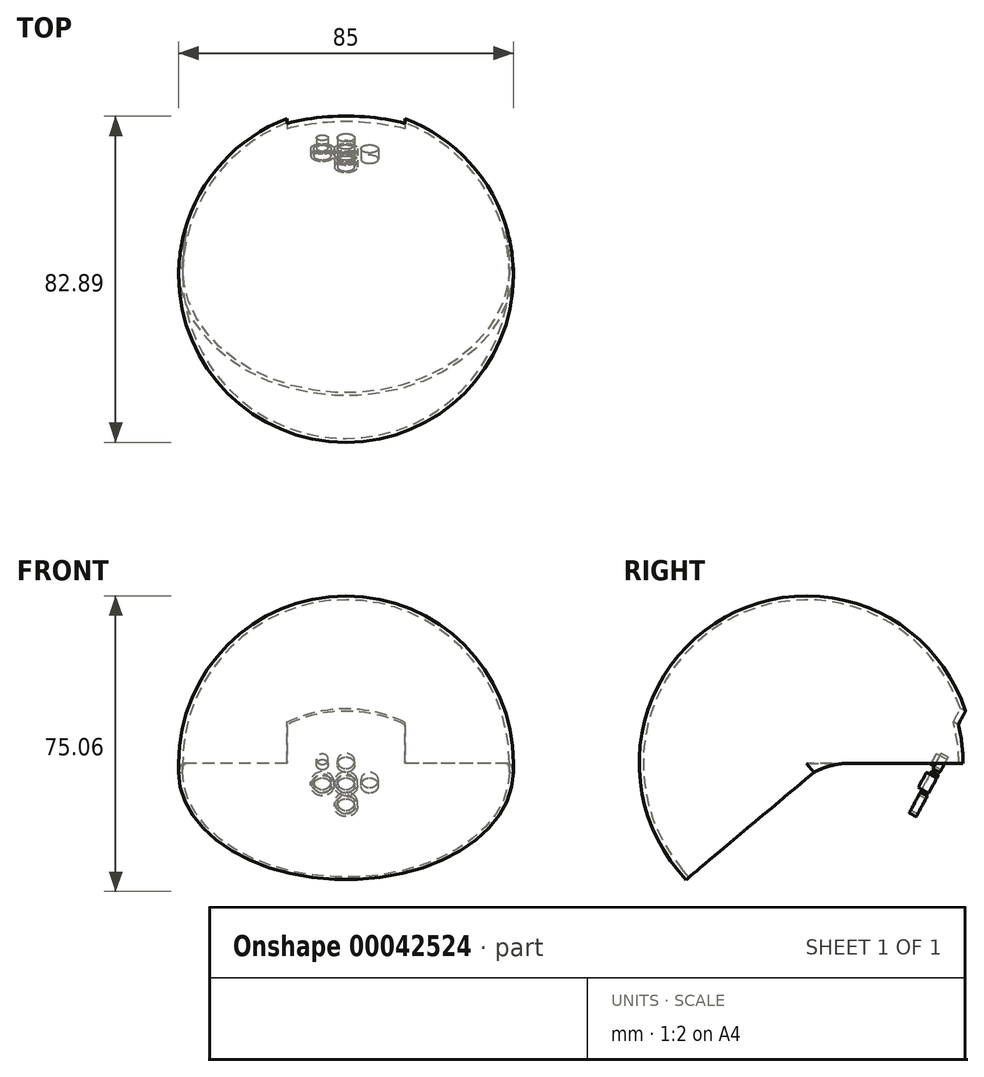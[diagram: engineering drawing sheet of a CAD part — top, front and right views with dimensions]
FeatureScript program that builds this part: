
annotation { "Feature Type Name" : "Feature", "Feature Type Description" : "" }
export const myFeature = defineFeature(function(context is Context, id is Id, definition is map)
    precondition{}
    {
        {
            var Q0;
            Q0=qCreatedBy(makeId("Top.planeOp"),FACE);
            var sketch = newSketch(context, id + "F0", { "sketchPlane" : qUnion([Q0])});
            skArc(sketch, "E0", {"start": v(42.5, 0) * mm, "mid": v(0, 42.5) * mm, "end": v(-42.5, 0) * mm});
            skLineSegment(sketch, "E1", {"start": v(-57, 0) * mm, "end": v(51.83, 0) * mm});
            skSolve(sketch);
        }
        {
            var Q0;
            {var subQ1=sQuery(id+"F0.wireOp",EDGE,"E0");Q0=makeQuery(id+"F0.imprint","IMPRINT",FACE,{"disambiguationData":[TD([[makeQuery(id+"F0.imprint","IMPRINT",EDGE,{"derivedFrom":subQ1}),1.0]])]});}
            var Q1;
            Q1=sQuery(id+"F0.wireOp",EDGE,"E1");
            revolve(context, id + "F1", {"entities" : qUnion([Q0]), "axis" : qUnion([Q1]), "revolveType" : RevolveType.ONE_DIRECTION, "angle" : 220 * degree});
        }
        {
            var Q0;
            Q0=makeQuery(id+"F1.opRevolve","CAP_FACE",FACE,{"disambiguationData":[OSD([sQuery(id+"F0.wireOp",EDGE,"E0"),sQuery(id+"F0.wireOp",EDGE,"E1")])],"isStart":true});
            var Q1;
            Q1=makeQuery(id+"F1.opRevolve","CAP_FACE",FACE,{"disambiguationData":[OSD([sQuery(id+"F0.wireOp",EDGE,"E0"),sQuery(id+"F0.wireOp",EDGE,"E1")])],"isStart":false});
            shell(context, id + "F2", {"entities" : qUnion([Q0, Q1]), "thickness" : 1 * mm});
        }
        {
            var Q0;
            Q0=makeQuery(id+"F1.opRevolve","CAP_FACE",FACE,{"disambiguationData":[OSD([sQuery(id+"F0.wireOp",EDGE,"E0"),sQuery(id+"F0.wireOp",EDGE,"E1")])],"isStart":false});
            extrude(context, id + "F3", {"entities" : qUnion([Q0]), "operationType" : NewBodyOperationType.ADD, "depth" : 3 * mm});
        }
        {
            var Q0;
            Q0=qCreatedBy(makeId("Top.planeOp"),FACE);
            cPlane(context, id + "F4", {"entities" : qUnion([Q0]), "cplaneType" : CPlaneType.OFFSET, "offset" : 28 * mm, "oppositeDirection" : true, "width" : 150 * mm, "height" : 150 * mm});
        }
        {
            var Q0;
            Q0=qCreatedBy(id+"F4.planeOp",FACE);
            var sketch = newSketch(context, id + "F5", { "sketchPlane" : qUnion([Q0])});
            skLineSegment(sketch, "E2", {"start": v(0, 0) * mm, "end": v(0, -48.92) * mm, "construction": true});
            skPoint(sketch, "E3", {"position": v(0, -28.7) * mm});
            skPoint(sketch, "E4", {"position": v(0, -35.7) * mm});
            skLineSegment(sketch, "E5", {"start": v(0, -35.7) * mm, "end": v(-10, -35.7) * mm});
            skPoint(sketch, "E6", {"position": v(0, -26.4) * mm});
            skLineSegment(sketch, "E7", {"start": v(0, -26.4) * mm, "end": v(-10, -26.4) * mm});
            skLineSegment(sketch, "E8", {"start": v(-10, -26.4) * mm, "end": v(-10, -35.7) * mm});
            skLineSegment(sketch, "E9.MirrorCS", {"start": v(0, -35.7) * mm, "end": v(10, -35.7) * mm});
            skLineSegment(sketch, "E10.MirrorCS", {"start": v(10, -26.4) * mm, "end": v(10, -35.7) * mm});
            skLineSegment(sketch, "E11.MirrorCS", {"start": v(0, -26.4) * mm, "end": v(10, -26.4) * mm});
            skSolve(sketch);
        }
        {
            var Q0;
            Q0=makeQuery(id+"F1.opRevolve","CAP_FACE",FACE,{"disambiguationData":[OSD([sQuery(id+"F0.wireOp",EDGE,"E0"),sQuery(id+"F0.wireOp",EDGE,"E1")])],"isStart":true});
            cPlane(context, id + "F6", {"entities" : qUnion([Q0]), "cplaneType" : CPlaneType.OFFSET, "offset" : 0 * mm, "width" : 150 * mm, "height" : 150 * mm});
        }
        {
            var Q0;
            Q0=qCreatedBy(id+"F6.planeOp",FACE);
            var sketch = newSketch(context, id + "F7", { "sketchPlane" : qUnion([Q0])});
            skLineSegment(sketch, "E12", {"start": v(0, 0) * mm, "end": v(40, 0) * mm});
            skLineSegment(sketch, "E13.MirrorCS", {"start": v(0, 0) * mm, "end": v(-40, 0) * mm});
            skSolve(sketch);
        }
        {
            var Q0;
            Q0=sQuery(id+"F7.wireOp",EDGE,"E12");
            cPlane(context, id + "F8", {"entities" : qUnion([Q0]), "cplaneType" : CPlaneType.LINE_ANGLE, "offset" : 150 * mm, "angle" : 62 * degree, "width" : 150 * mm, "height" : 150 * mm});
        }
        {
            var Q0;
            Q0=qCreatedBy(id+"F8.planeOp",FACE);
            var sketch = newSketch(context, id + "F9", { "sketchPlane" : qUnion([Q0])});
            skLineSegment(sketch, "E14", {"start": v(0, 0) * mm, "end": v(0, 38) * mm, "construction": true});
            skPoint(sketch, "E15", {"position": v(0, 33) * mm});
            skPoint(sketch, "E16", {"position": v(0, 31) * mm});
            skLineSegment(sketch, "E17", {"start": v(0, 31) * mm, "end": v(-15, 31) * mm});
            skLineSegment(sketch, "E18", {"start": v(-15, 31) * mm, "end": v(-15, 28) * mm});
            skLineSegment(sketch, "E19", {"start": v(-15, 28) * mm, "end": v(0, 28) * mm});
            skLineSegment(sketch, "E20.MirrorCS", {"start": v(15, 28) * mm, "end": v(0, 28) * mm});
            skLineSegment(sketch, "E21.MirrorCS", {"start": v(15, 31) * mm, "end": v(15, 28) * mm});
            skLineSegment(sketch, "E22.MirrorCS", {"start": v(0, 31) * mm, "end": v(15, 31) * mm});
            skSolve(sketch);
        }
        {
            var Q0;
            Q0=makeQuery(id+"F9.imprint","IMPRINT",FACE,{"disambiguationData":[TD([[makeQuery(id+"F9.imprint","IMPRINT",EDGE,{"derivedFrom":sQuery(id+"F9.wireOp",EDGE,"E17")}),1.0]])]});
            var Q1;
            Q1=makeQuery(id+"F2.opShell","OFFSET_FACE",FACE,{"disambiguationData":[OSD([sQuery(id+"F0.wireOp",EDGE,"E0")])]});
            var Q2;
            Q2=makeQuery(id+"F1.opRevolve","SWEPT_BODY",BODY,{"disambiguationData":[OSD([sQuery(id+"F0.wireOp",EDGE,"E0"),sQuery(id+"F0.wireOp",EDGE,"E1")])]});
            extrude(context, id + "F10", {"entities" : qUnion([Q0]), "operationType" : NewBodyOperationType.ADD, "endBound" : BoundingType.UP_TO_SURFACE, "endBoundEntityFace" : qUnion([Q1]), "endBoundEntityBody" : qUnion([Q2]), "depth" : 25 * mm});
        }
        {
            var Q0;
            Q0=makeQuery(id+"F10.opExtrude","SWEPT_FACE",FACE,{"disambiguationData":[OSD([sQuery(id+"F9.wireOp",EDGE,"E19"),sQuery(id+"F9.wireOp",EDGE,"E20.MirrorCS")])]});
            var sketch = newSketch(context, id + "F11", { "sketchPlane" : qUnion([Q0])});
            skPoint(sketch, "E23", {"position": v(0, 0) * mm});
            skLineSegment(sketch, "E24", {"start": v(0, 0) * mm, "end": v(0, 30.63) * mm, "construction": true});
            skCircle(sketch, "E25", {"center": v(0, 4.05) * mm, "radius": 2.95 * mm});
            skCircle(sketch, "E26", {"center": v(0, 4.05) * mm, "radius": 2.2 * mm});
            skCircle(sketch, "E27", {"center": v(0, 10.05) * mm, "radius": 2.95 * mm});
            skCircle(sketch, "E28", {"center": v(0, 10.05) * mm, "radius": 2.2 * mm});
            skCircle(sketch, "E29", {"center": v(-6, 10.05) * mm, "radius": 2.95 * mm});
            skLineSegment(sketch, "E30", {"start": v(0, 10.05) * mm, "end": v(-6, 10.05) * mm, "construction": true});
            skCircle(sketch, "E31", {"center": v(-6, 10.05) * mm, "radius": 2.2 * mm});
            skCircle(sketch, "E32.MirrorC", {"center": v(6, 10.05) * mm, "radius": 2.95 * mm});
            skCircle(sketch, "E33.MirrorC", {"center": v(6, 10.05) * mm, "radius": 2.2 * mm});
            skCircle(sketch, "E34.MirrorC", {"center": v(0, 16.05) * mm, "radius": 2.2 * mm});
            skCircle(sketch, "E35.MirrorC", {"center": v(0, 16.05) * mm, "radius": 2.95 * mm});
            skPoint(sketch, "E36", {"position": v(6, 16.05) * mm});
            skCircle(sketch, "E37", {"center": v(6, 16.05) * mm, "radius": 1.5 * mm});
            skCircle(sketch, "E38.MirrorC", {"center": v(-6, 16.05) * mm, "radius": 1.5 * mm});
            skSolve(sketch);
        }
        {
            var Q0;
            Q0=makeQuery(id+"F11.imprint","IMPRINT",FACE,{"disambiguationData":[TD([[makeQuery(id+"F11.imprint","IMPRINT",EDGE,{"derivedFrom":sQuery(id+"F11.wireOp",EDGE,"E28")}),1.0]])]});
            var Q1;
            Q1=makeQuery(id+"F11.imprint","IMPRINT",FACE,{"disambiguationData":[TD([[makeQuery(id+"F11.imprint","IMPRINT",EDGE,{"derivedFrom":sQuery(id+"F11.wireOp",EDGE,"E34.MirrorC")}),-1.0]])]});
            var Q2;
            Q2=makeQuery(id+"F11.imprint","IMPRINT",FACE,{"disambiguationData":[TD([[makeQuery(id+"F11.imprint","IMPRINT",EDGE,{"derivedFrom":sQuery(id+"F11.wireOp",EDGE,"E33.MirrorC")}),-1.0]])]});
            var Q3;
            Q3=makeQuery(id+"F11.imprint","IMPRINT",FACE,{"disambiguationData":[TD([[makeQuery(id+"F11.imprint","IMPRINT",EDGE,{"derivedFrom":sQuery(id+"F11.wireOp",EDGE,"E31")}),1.0]])]});
            var Q4;
            Q4=makeQuery(id+"F11.imprint","IMPRINT",FACE,{"disambiguationData":[TD([[makeQuery(id+"F11.imprint","IMPRINT",EDGE,{"derivedFrom":sQuery(id+"F11.wireOp",EDGE,"E26")}),1.0]])]});
            extrude(context, id + "F12", {"entities" : qUnion([Q0, Q1, Q2, Q3, Q4]), "operationType" : NewBodyOperationType.REMOVE, "endBound" : BoundingType.UP_TO_NEXT, "oppositeDirection" : true, "depth" : 25 * mm});
        }
        {
            var Q0;
            Q0=makeQuery(id+"F11.imprint","IMPRINT",FACE,{"disambiguationData":[TD([[makeQuery(id+"F11.imprint","IMPRINT",EDGE,{"derivedFrom":sQuery(id+"F11.wireOp",EDGE,"E29")}),1.0]])]});
            var Q1;
            Q1=makeQuery(id+"F11.imprint","IMPRINT",FACE,{"disambiguationData":[TD([[makeQuery(id+"F11.imprint","IMPRINT",EDGE,{"derivedFrom":sQuery(id+"F11.wireOp",EDGE,"E27")}),1.0]])]});
            var Q2;
            Q2=makeQuery(id+"F11.imprint","IMPRINT",FACE,{"disambiguationData":[TD([[makeQuery(id+"F11.imprint","IMPRINT",EDGE,{"derivedFrom":sQuery(id+"F11.wireOp",EDGE,"E32.MirrorC")}),-1.0]])]});
            var Q3;
            Q3=makeQuery(id+"F11.imprint","IMPRINT",FACE,{"disambiguationData":[TD([[makeQuery(id+"F11.imprint","IMPRINT",EDGE,{"derivedFrom":sQuery(id+"F11.wireOp",EDGE,"E34.MirrorC")}),1.0]])]});
            var Q4;
            Q4=makeQuery(id+"F11.imprint","IMPRINT",FACE,{"disambiguationData":[TD([[makeQuery(id+"F11.imprint","IMPRINT",EDGE,{"derivedFrom":sQuery(id+"F11.wireOp",EDGE,"E25")}),1.0]])]});
            extrude(context, id + "F13", {"entities" : qUnion([Q0, Q1, Q2, Q3, Q4]), "operationType" : NewBodyOperationType.REMOVE, "oppositeDirection" : true, "depth" : 1 * mm});
        }
        {
            var Q0;
            Q0=makeQuery(id+"F11.imprint","IMPRINT",FACE,{"disambiguationData":[TD([[makeQuery(id+"F11.imprint","IMPRINT",EDGE,{"derivedFrom":sQuery(id+"F11.wireOp",EDGE,"E25")}),-1.0]])]});
            cPlane(context, id + "F14", {"entities" : qUnion([Q0]), "cplaneType" : CPlaneType.OFFSET, "offset" : 80 * mm, "width" : 150 * mm, "height" : 150 * mm});
        }
        {
            var Q0;
            Q0=qCreatedBy(id+"F14.planeOp",FACE);
            var sketch = newSketch(context, id + "F15", { "sketchPlane" : qUnion([Q0])});
            skPoint(sketch, "E39", {"position": v(1.77, 0) * mm});
            skLineSegment(sketch, "E40", {"start": v(1.77, 0) * mm, "end": v(1.77, 65.04) * mm, "construction": true});
            skCircle(sketch, "E41", {"center": v(1.77, 9.5) * mm, "radius": 7.5 * mm});
            skCircle(sketch, "E42", {"center": v(1.77, 9.5) * mm, "radius": 8 * mm});
            skSolve(sketch);
        }
        {
            var Q0;
            {var subQ0=sQuery(id+"F0.wireOp",EDGE,"E1");var subQ1=makeQuery(id+"F2.opShell","OFFSET_EDGE",EDGE,{"disambiguationData":[OSD([subQ0])]});Q0=makeQuery(id+"F3.boolean.opBoolean","MERGE",EDGE,{"derivedFrom":[subQ1,makeQuery(id+"F3.opExtrude","CAP_EDGE",EDGE,{"disambiguationData":[OSD([subQ0]),TDD([subQ1])],"isStart":true})]});}
            var Q1;
            {var subQ0=sQuery(id+"F0.wireOp",EDGE,"E1");var subQ1=makeQuery(id+"F1.opRevolve","CAP_EDGE",EDGE,{"disambiguationData":[OSD([subQ0])],"isStart":true});Q1=makeQuery(id+"F3.boolean.opBoolean","MERGE",EDGE,{"derivedFrom":[subQ1,makeQuery(id+"F3.opExtrude","CAP_EDGE",EDGE,{"disambiguationData":[OSD([subQ0]),TDD([subQ1])],"isStart":true})]});}
            fillet(context, id + "F16", {"entities" : qUnion([Q0, Q1]), "radius" : 20 * mm, "tangentPropagation" : true, "allowEdgeOverflow" : false});
        }
        {
            var Q0;
            Q0=qCreatedBy(id+"F14.planeOp",FACE);
            cPlane(context, id + "F17", {"entities" : qUnion([Q0]), "cplaneType" : CPlaneType.OFFSET, "offset" : 20 * mm, "oppositeDirection" : true, "width" : 150 * mm, "height" : 150 * mm});
        }
        {
            var Q0;
            Q0=makeQuery(id+"F11.imprint","IMPRINT",FACE,{"disambiguationData":[TD([[makeQuery(id+"F11.imprint","IMPRINT",EDGE,{"derivedFrom":sQuery(id+"F11.wireOp",EDGE,"E38.MirrorC")}),-1.0]])]});
            var Q1;
            Q1=makeQuery(id+"F11.imprint","IMPRINT",FACE,{"disambiguationData":[TD([[makeQuery(id+"F11.imprint","IMPRINT",EDGE,{"derivedFrom":sQuery(id+"F11.wireOp",EDGE,"E37")}),1.0]])]});
            extrude(context, id + "F18", {"entities" : qUnion([Q0, Q1]), "operationType" : NewBodyOperationType.REMOVE, "oppositeDirection" : true, "depth" : 25 * mm});
        }
    });
